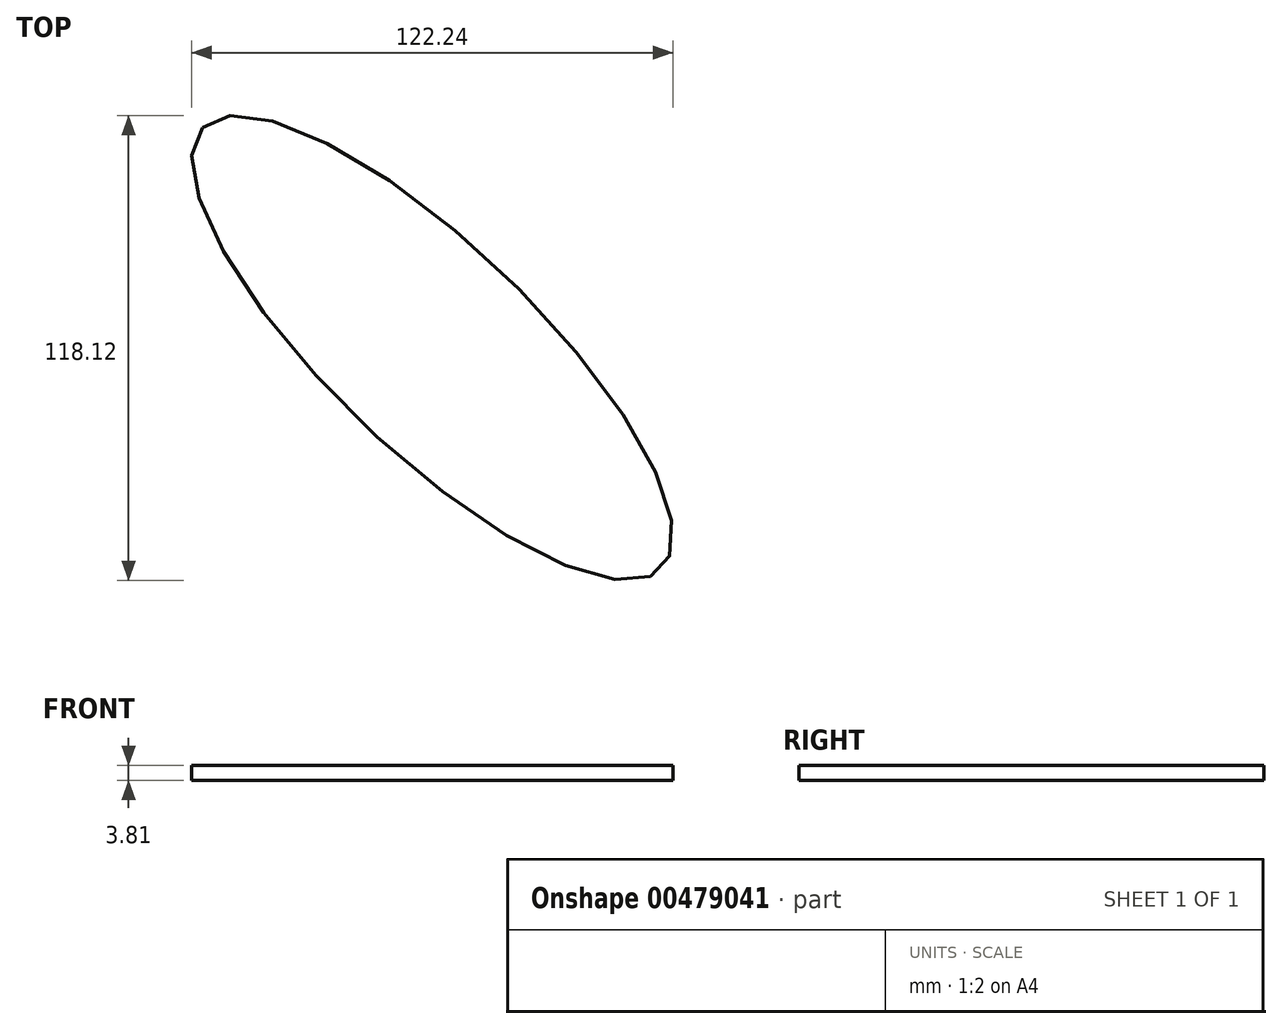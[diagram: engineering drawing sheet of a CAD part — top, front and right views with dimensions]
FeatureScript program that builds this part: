
annotation { "Feature Type Name" : "Feature", "Feature Type Description" : "" }
export const myFeature = defineFeature(function(context is Context, id is Id, definition is map)
    precondition{}
    {
        {
            var Q0;
            Q0=qCreatedBy(makeId("Top.planeOp"),FACE);
            var sketch = newSketch(context, id + "F0", { "sketchPlane" : qUnion([Q0])});
            skEllipse(sketch, "E0", {"center": v(0, 0) * mm, "majorRadius": 80.9 * mm, "minorRadius": 26.08 * mm, "majorAxis": v(-0.72, 0.7)});
            skSolve(sketch);
        }
        {
            var Q0;
            Q0=makeQuery(id+"F0.imprint","IMPRINT",FACE,{"disambiguationData":[TD([[makeQuery(id+"F0.imprint","IMPRINT",EDGE,{"derivedFrom":sQuery(id+"F0.wireOp",EDGE,"E0")}),1.0]])]});
            extrude(context, id + "F1", {"entities" : qUnion([Q0]), "depth" : 3.8 * mm});
        }
    });
